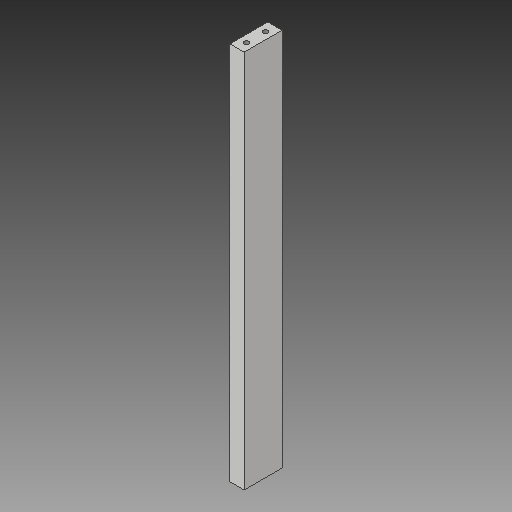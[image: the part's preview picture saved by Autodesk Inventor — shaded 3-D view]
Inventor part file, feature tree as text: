
AUTODESK INVENTOR PART (.ipt)
format: ipt  version: 2019 (Build 230136000, 136)  size: 108,544 bytes
history: native  units: in
note: dims shown in document units (in); Inventor stores cm internally (conversion verified against a paired STEP export)
features: sketch x3, hole x2, extrude x1
ambient origin geometry x8: Origin, YZ Plane, XZ Plane, XY Plane, X Axis, Y Axis, Z Axis, Center Point
bodies: Solid1 (feature_tree)
feature tree (6):
  extrude  "Extrusion1"  Depth=10.0in
  hole  "Hole1"  [1 undecoded]
  hole  "Hole2"  [1 undecoded]
  sketch  "Sketch1"  dims[d0=0.375in d1=10.0in]
  sketch  "Sketch2"  dims[d2=1.0in d3=0.0in]
  sketch  "Sketch3"  dims[d6=0.13in d7=0.25in d8=0.375in d9=0.25in d10=0.5635in d11=0.3in d12=0.8108in d14=0.13in d15=0.25in d16=0.375in d17=0.25in d18=0.5635in d19=0.3in d20=0.8108in]
note: 2 required parameter values undecoded (feature->parameter linkage not recoverable at this tier; creation-order binding heuristic only, values carry confidence <= 0.55)
